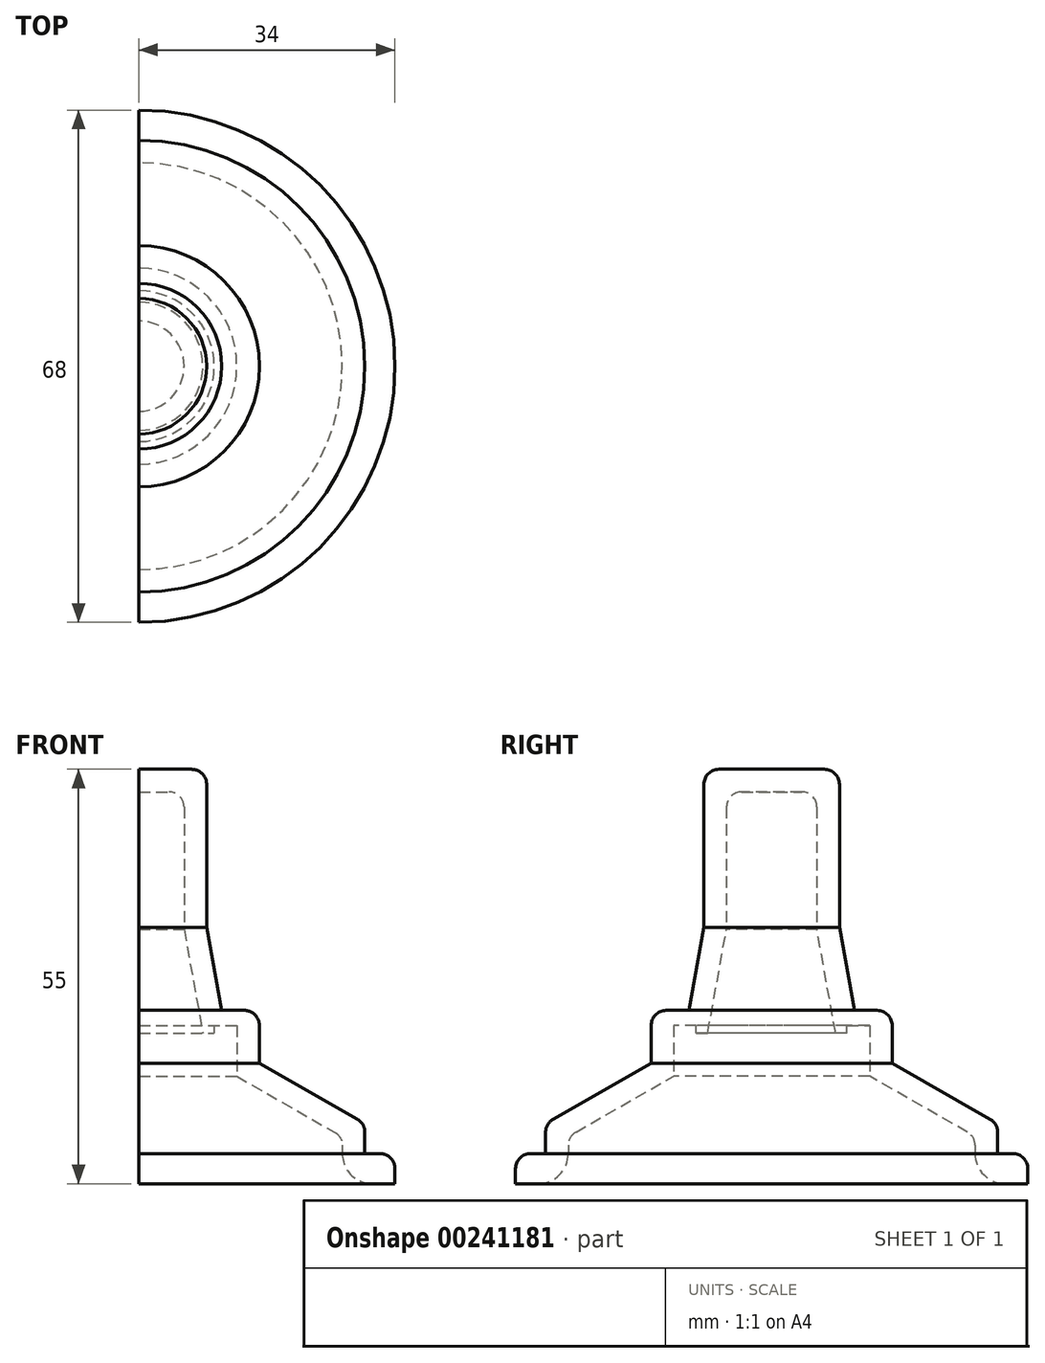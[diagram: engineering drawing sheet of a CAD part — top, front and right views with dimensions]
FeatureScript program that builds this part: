
annotation { "Feature Type Name" : "Feature", "Feature Type Description" : "" }
export const myFeature = defineFeature(function(context is Context, id is Id, definition is map)
    precondition{}
    {
        {
            var Q0;
            Q0=qCreatedBy(makeId("Front.planeOp"),FACE);
            var sketch = newSketch(context, id + "F0", { "sketchPlane" : qUnion([Q0])});
            skLineSegment(sketch, "E0", {"start": v(-34, -27.18) * mm, "end": v(34, -27.18) * mm});
            skLineSegment(sketch, "E1", {"start": v(-9, 27.82) * mm, "end": v(7, 27.82) * mm});
            skLineSegment(sketch, "E2", {"start": v(0, -27.18) * mm, "end": v(0, 27.82) * mm});
            skLineSegment(sketch, "E3", {"start": v(34, -27.18) * mm, "end": v(34, -25.18) * mm});
            skLineSegment(sketch, "E4", {"start": v(32, -23.18) * mm, "end": v(30, -23.18) * mm});
            skLineSegment(sketch, "E5", {"start": v(30, -23.18) * mm, "end": v(30, -20.34) * mm});
            skLineSegment(sketch, "E6", {"start": v(29, -18.6) * mm, "end": v(16, -11.18) * mm});
            skLineSegment(sketch, "E7", {"start": v(16, -11.18) * mm, "end": v(16, -6.18) * mm});
            skLineSegment(sketch, "E8", {"start": v(14, -4.18) * mm, "end": v(11, -4.18) * mm});
            skLineSegment(sketch, "E9", {"start": v(11, -4.18) * mm, "end": v(9, 6.82) * mm});
            skLineSegment(sketch, "E10", {"start": v(9, 25.82) * mm, "end": v(9, 6.82) * mm});
            skPoint(sketch, "E11.visualSharp", {"position": v(16, -4.18) * mm});
            skArc(sketch, "E11.filletArc", {"start": v(16, -6.18) * mm, "mid": v(15.41, -4.77) * mm, "end": v(14, -4.18) * mm});
            skPoint(sketch, "E12.visualSharp", {"position": v(9, 27.82) * mm});
            skArc(sketch, "E12.filletArc", {"start": v(9, 25.82) * mm, "mid": v(8.41, 27.23) * mm, "end": v(7, 27.82) * mm});
            skPoint(sketch, "E13.visualSharp", {"position": v(30, -19.18) * mm});
            skArc(sketch, "E13.filletArc", {"start": v(30, -20.34) * mm, "mid": v(29.73, -19.34) * mm, "end": v(29, -18.6) * mm});
            skPoint(sketch, "E14.visualSharp", {"position": v(34, -23.18) * mm});
            skArc(sketch, "E14.filletArc", {"start": v(34, -25.18) * mm, "mid": v(33.41, -23.77) * mm, "end": v(32, -23.18) * mm});
            skLineSegment(sketch, "E15", {"start": v(34, -27.18) * mm, "end": v(31, -27.18) * mm});
            skLineSegment(sketch, "E16.0", {"start": v(13, -12.92) * mm, "end": v(13, -7.18) * mm});
            skLineSegment(sketch, "E16.1", {"start": v(26, -20.35) * mm, "end": v(13, -12.92) * mm});
            skLineSegment(sketch, "E17", {"start": v(27, -22.08) * mm, "end": v(27, -23.18) * mm});
            skPoint(sketch, "E18.visualSharp", {"position": v(27, -20.92) * mm});
            skArc(sketch, "E18.filletArc", {"start": v(27, -22.08) * mm, "mid": v(26.73, -21.08) * mm, "end": v(26, -20.35) * mm});
            skArc(sketch, "E19", {"start": v(27, -23.18) * mm, "mid": v(28.17, -26) * mm, "end": v(31, -27.18) * mm});
            skLineSegment(sketch, "E20", {"start": v(10, -7.18) * mm, "end": v(0, -7.18) * mm});
            skLineSegment(sketch, "E21", {"start": v(10, -7.18) * mm, "end": v(10, -6.18) * mm});
            skLineSegment(sketch, "E22", {"start": v(10, -6.18) * mm, "end": v(13, -6.18) * mm});
            skLineSegment(sketch, "E23", {"start": v(13, -6.18) * mm, "end": v(13, -7.18) * mm});
            skLineSegment(sketch, "E24.0", {"start": v(8.5, -7.18) * mm, "end": v(6, 6.55) * mm});
            skLineSegment(sketch, "E24.1", {"start": v(6, 22.82) * mm, "end": v(6, 6.55) * mm});
            skLineSegment(sketch, "E24.2", {"start": v(-9, 24.82) * mm, "end": v(4, 24.82) * mm});
            skPoint(sketch, "E25.visualSharp", {"position": v(6, 24.82) * mm});
            skArc(sketch, "E25.filletArc", {"start": v(6, 22.82) * mm, "mid": v(5.41, 24.23) * mm, "end": v(4, 24.82) * mm});
            skSolve(sketch);
        }
        {
            var Q0;
            Q0=makeQuery(id+"F0.imprint","IMPRINT",FACE,{"disambiguationData":[TD([[makeQuery(id+"F0.imprint","IMPRINT",EDGE,{"derivedFrom":sQuery(id+"F0.wireOp",EDGE,"E3")}),1.0]])]});
            var Q1;
            Q1=sQuery(id+"F0.wireOp",EDGE,"E2");
            revolve(context, id + "F1", {"entities" : qUnion([Q0]), "axis" : qUnion([Q1]), "revolveType" : RevolveType.SYMMETRIC, "angle" : 180 * degree});
        }
    });
